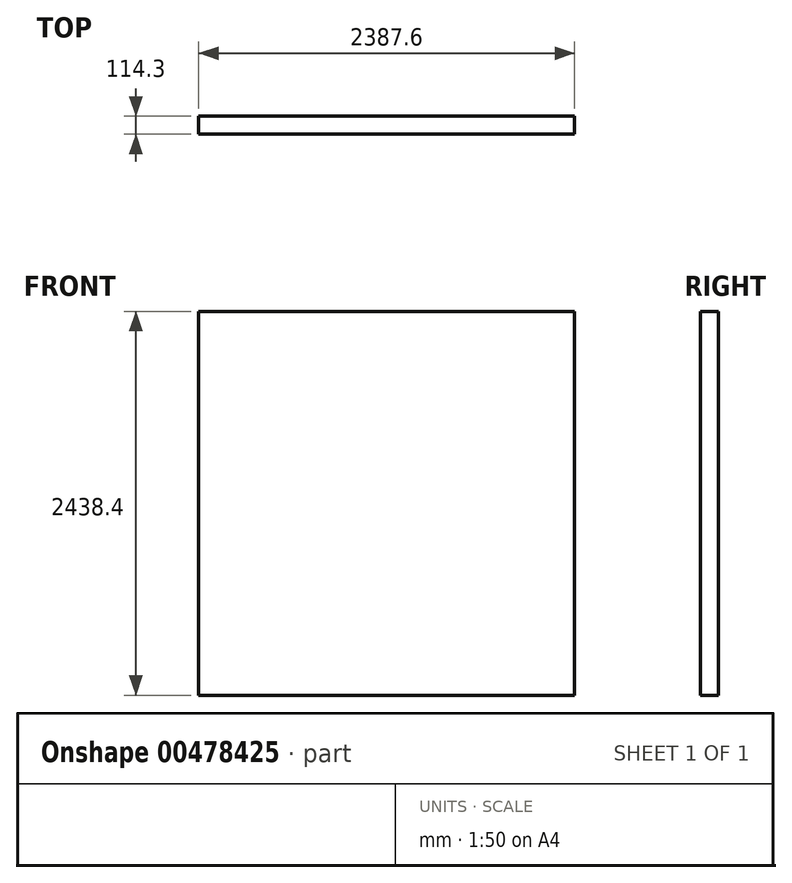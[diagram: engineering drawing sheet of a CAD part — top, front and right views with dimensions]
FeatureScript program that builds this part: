
annotation { "Feature Type Name" : "Feature", "Feature Type Description" : "" }
export const myFeature = defineFeature(function(context is Context, id is Id, definition is map)
    precondition{}
    {
        {
            var Q0;
            Q0=qCreatedBy(makeId("Top.planeOp"),FACE);
            var sketch = newSketch(context, id + "F0", { "sketchPlane" : qUnion([Q0])});
            skLineSegment(sketch, "E0.bottom", {"start": v(1193.8, -57.15) * mm, "end": v(-1193.8, -57.15) * mm});
            skLineSegment(sketch, "E0.top", {"start": v(1193.8, 57.15) * mm, "end": v(-1193.8, 57.15) * mm});
            skLineSegment(sketch, "E0.left", {"start": v(1193.8, -57.15) * mm, "end": v(1193.8, 57.15) * mm});
            skLineSegment(sketch, "E0.right", {"start": v(-1193.8, -57.15) * mm, "end": v(-1193.8, 57.15) * mm});
            skPoint(sketch, "E0.middle", {"position": v(0, 0) * mm});
            skSolve(sketch);
        }
        {
            var Q0;
            Q0 = qSketchRegion(id + "F0", true);
            extrude(context, id + "F1", {"entities" : qUnion([Q0]), "depth" : 2438.4 * mm});
        }
    });
